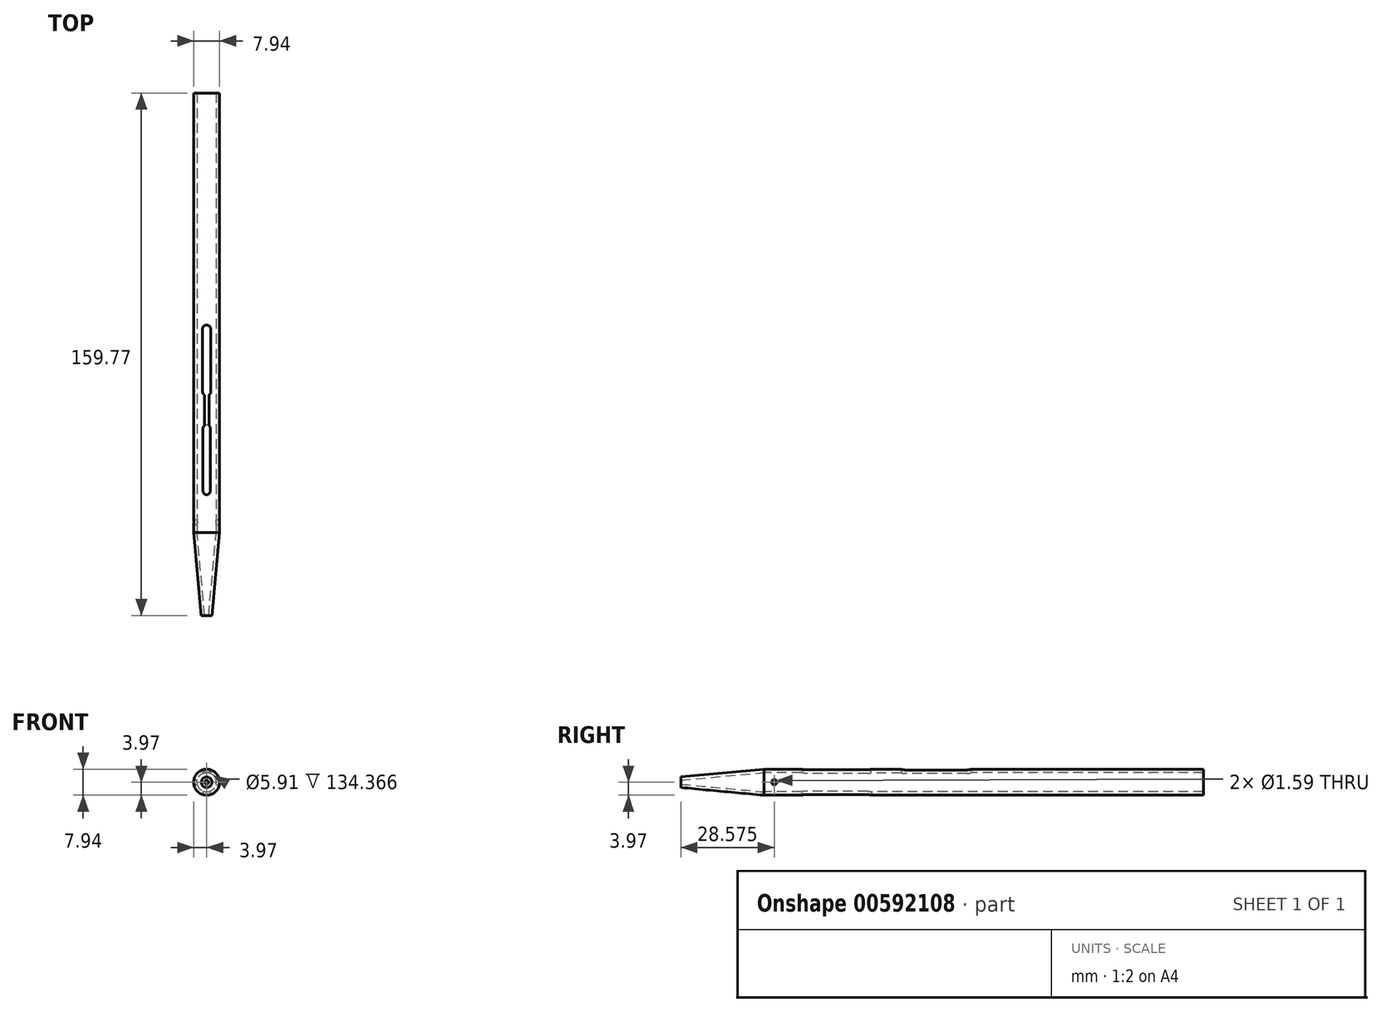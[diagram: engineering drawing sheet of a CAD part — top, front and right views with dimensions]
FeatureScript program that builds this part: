
annotation { "Feature Type Name" : "Feature", "Feature Type Description" : "" }
export const myFeature = defineFeature(function(context is Context, id is Id, definition is map)
    precondition{}
    {
        {
            var Q0;
            Q0=qCreatedBy(makeId("Front.planeOp"),FACE);
            var sketch = newSketch(context, id + "F0", { "sketchPlane" : qUnion([Q0])});
            skCircle(sketch, "E0", {"center": v(0, 0) * mm, "radius": 3.97 * mm});
            skCircle(sketch, "E1.0", {"center": v(0, 0) * mm, "radius": 2.95 * mm});
            skSolve(sketch);
        }
        {
            var Q0;
            Q0 = qSketchRegion(id + "F0", true);
            extrude(context, id + "F1", {"entities" : qUnion([Q0]), "oppositeDirection" : true, "depth" : 134.37 * mm, "offsetDistance" : 25.4 * mm});
        }
        {
            var Q0;
            Q0=qCreatedBy(makeId("Top.planeOp"),FACE);
            var sketch = newSketch(context, id + "F2", { "sketchPlane" : qUnion([Q0])});
            skLineSegment(sketch, "E2", {"start": v(0, 31.75) * mm, "end": v(0, 12.7) * mm});
            skArc(sketch, "E3.0.startCap", {"start": v(-1.14, 31.75) * mm, "mid": v(0, 32.9) * mm, "end": v(1.14, 31.75) * mm});
            skArc(sketch, "E3.0.endCap", {"start": v(1.14, 12.7) * mm, "mid": v(0, 11.56) * mm, "end": v(-1.14, 12.7) * mm});
            skLineSegment(sketch, "E3.0.left", {"start": v(1.14, 31.75) * mm, "end": v(1.14, 12.7) * mm});
            skLineSegment(sketch, "E3.0.right", {"start": v(-1.14, 31.75) * mm, "end": v(-1.14, 12.7) * mm});
            skSolve(sketch);
        }
        {
            var Q0;
            Q0 = qSketchRegion(id + "F2", true);
            extrude(context, id + "F3", {"entities" : qUnion([Q0]), "operationType" : NewBodyOperationType.REMOVE, "endBound" : BoundingType.THROUGH_ALL, "depth" : 25.4 * mm, "offsetDistance" : 25.4 * mm, "hasSecondDirection" : true, "secondDirectionBound" : SecondDirectionBoundingType.THROUGH_ALL, "secondDirectionOppositeDirection" : true, "secondDirectionDepth" : 25.4 * mm});
        }
        {
            var Q0;
            Q0=qCreatedBy(makeId("Top.planeOp"),FACE);
            var sketch = newSketch(context, id + "F4", { "sketchPlane" : qUnion([Q0])});
            skLineSegment(sketch, "E4", {"start": v(0, 62.17) * mm, "end": v(0, 43.12) * mm, "construction": true});
            skArc(sketch, "E5.0.startCap", {"start": v(-1.27, 62.17) * mm, "mid": v(0, 63.44) * mm, "end": v(1.27, 62.17) * mm});
            skArc(sketch, "E5.0.endCap", {"start": v(1.27, 43.12) * mm, "mid": v(1.12, 42.51) * mm, "end": v(0.7, 42.05) * mm});
            skLineSegment(sketch, "E5.0.left", {"start": v(1.27, 62.17) * mm, "end": v(1.27, 43.12) * mm});
            skLineSegment(sketch, "E5.0.right", {"start": v(-1.27, 62.17) * mm, "end": v(-1.27, 43.12) * mm});
            skLineSegment(sketch, "E6.top", {"start": v(-0.7, 32) * mm, "end": v(0.7, 32) * mm});
            skLineSegment(sketch, "E6.left", {"start": v(-0.7, 42.05) * mm, "end": v(-0.7, 32) * mm});
            skLineSegment(sketch, "E6.right", {"start": v(0.7, 42.05) * mm, "end": v(0.7, 32) * mm});
            skPoint(sketch, "E6.middle", {"position": v(0, 37.71) * mm});
            skPoint(sketch, "E7.orphan", {"position": v(-0.7, 43.43) * mm});
            skPoint(sketch, "E8.orphan", {"position": v(0.7, 43.43) * mm});
            skArc(sketch, "E9.trimOffspring", {"start": v(-0.7, 42.05) * mm, "mid": v(-1.12, 42.51) * mm, "end": v(-1.27, 43.12) * mm});
            skSolve(sketch);
        }
        {
            var Q0;
            Q0=qCreatedBy(makeId("Right.planeOp"),FACE);
            var sketch = newSketch(context, id + "F5", { "sketchPlane" : qUnion([Q0])});
            skLineSegment(sketch, "E10", {"start": v(-25.4, 1.62) * mm, "end": v(0, 3.97) * mm});
            skLineSegment(sketch, "E11.0", {"start": v(0, -3.97) * mm, "end": v(0, 3.97) * mm, "construction": true});
            skLineSegment(sketch, "E12", {"start": v(-25.4, 0) * mm, "end": v(0, 0) * mm, "construction": true});
            skLineSegment(sketch, "E13", {"start": v(0, 3.97) * mm, "end": v(0, 2.95) * mm});
            skLineSegment(sketch, "E14", {"start": v(0, 2.95) * mm, "end": v(-25.4, 0.6) * mm});
            skLineSegment(sketch, "E15", {"start": v(-25.4, 0.6) * mm, "end": v(-25.4, 1.62) * mm});
            skSolve(sketch);
        }
        {
            var Q0;
            Q0 = qSketchRegion(id + "F5", true);
            var Q1;
            Q1=sQuery(id+"F5.wireOp",EDGE,"E12");
            revolve(context, id + "F6", {"operationType" : NewBodyOperationType.ADD, "entities" : qUnion([Q0]), "axis" : qUnion([Q1]), "revolveType" : RevolveType.FULL});
        }
        {
            var Q0;
            Q0=qCreatedBy(makeId("Right.planeOp"),FACE);
            var sketch = newSketch(context, id + "F7", { "sketchPlane" : qUnion([Q0])});
            skCircle(sketch, "E16", {"center": v(3.18, 0) * mm, "radius": 0.8 * mm});
            skSolve(sketch);
        }
        {
            var Q0;
            Q0 = qSketchRegion(id + "F7", true);
            extrude(context, id + "F8", {"entities" : qUnion([Q0]), "operationType" : NewBodyOperationType.REMOVE, "endBound" : BoundingType.SYMMETRIC, "oppositeDirection" : true, "depth" : 25.4 * mm, "offsetDistance" : 25.4 * mm});
        }
        {
            var Q0;
            Q0 = qSketchRegion(id + "F4", true);
            extrude(context, id + "F9", {"entities" : qUnion([Q0]), "operationType" : NewBodyOperationType.REMOVE, "endBound" : BoundingType.THROUGH_ALL, "depth" : 25.4 * mm, "offsetDistance" : 25.4 * mm});
        }
        {
            var Q0;
            Q0=qCreatedBy(makeId("Right.planeOp"),FACE);
            var sketch = newSketch(context, id + "F10", { "sketchPlane" : qUnion([Q0])});
            skLineSegment(sketch, "E17", {"start": v(-9.53, 9.53) * mm, "end": v(9.53, -9.53) * mm});
            skLineSegment(sketch, "E18", {"start": v(0, 0) * mm, "end": v(21.81, 0) * mm, "construction": true});
            skSolve(sketch);
        }
        {
            var Q0;
            Q0=sQuery(id+"F10.wireOp",EDGE,"E17");
            extrude(context, id + "F11", {"bodyType" : ToolBodyType.SURFACE, "surfaceEntities" : qUnion([Q0]), "endBound" : BoundingType.SYMMETRIC, "depth" : 25.4 * mm, "offsetDistance" : 25.4 * mm});
        }
    });
